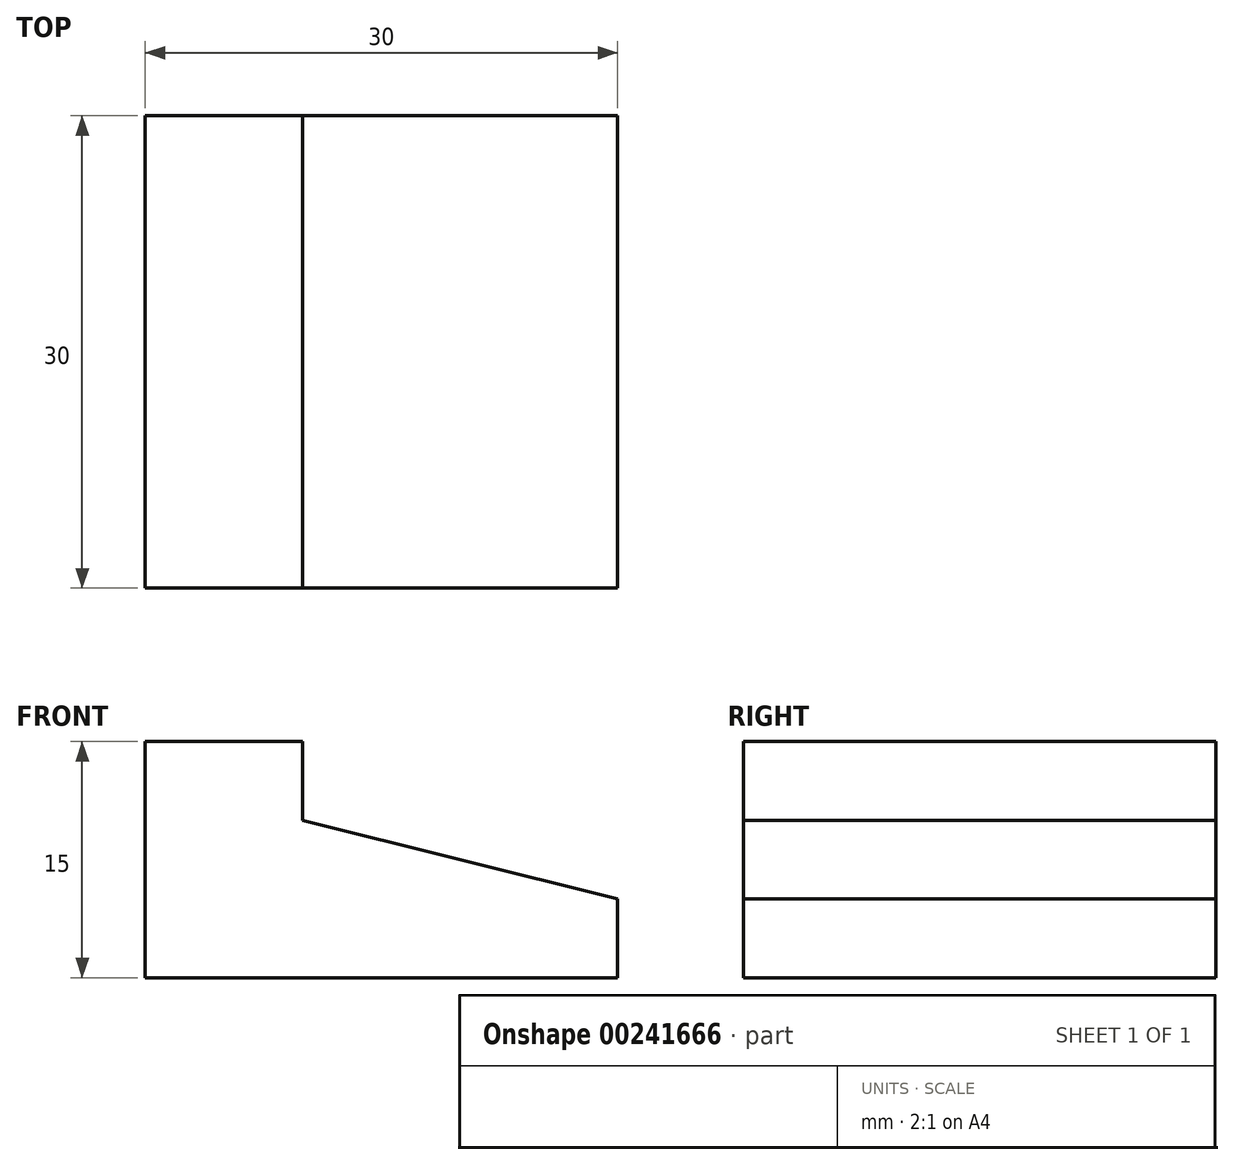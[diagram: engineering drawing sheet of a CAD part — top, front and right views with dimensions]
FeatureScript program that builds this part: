
annotation { "Feature Type Name" : "Feature", "Feature Type Description" : "" }
export const myFeature = defineFeature(function(context is Context, id is Id, definition is map)
    precondition{}
    {
        {
            var Q0;
            Q0=qCreatedBy(makeId("Top.planeOp"),FACE);
            var sketch = newSketch(context, id + "F0", { "sketchPlane" : qUnion([Q0])});
            skLineSegment(sketch, "E0.bottom", {"start": v(1.67, -3.94) * mm, "end": v(31.67, -3.94) * mm});
            skLineSegment(sketch, "E0.top", {"start": v(1.67, -33.94) * mm, "end": v(31.67, -33.94) * mm});
            skLineSegment(sketch, "E0.left", {"start": v(1.67, -3.94) * mm, "end": v(1.67, -33.94) * mm});
            skLineSegment(sketch, "E0.right", {"start": v(31.67, -3.94) * mm, "end": v(31.67, -33.94) * mm});
            skSolve(sketch);
        }
        {
            var Q0;
            Q0=makeQuery(id+"F0.imprint","IMPRINT",FACE,{"disambiguationData":[TD([[makeQuery(id+"F0.imprint","IMPRINT",EDGE,{"derivedFrom":sQuery(id+"F0.wireOp",EDGE,"E0.bottom")}),-1.0]])]});
            extrude(context, id + "F1", {"entities" : qUnion([Q0]), "depth" : 15 * mm});
        }
        {
            var Q0;
            Q0=makeQuery(id+"F1.opExtrude","SWEPT_FACE",FACE,{"disambiguationData":[OSD([sQuery(id+"F0.wireOp",EDGE,"E0.top")])]});
            var sketch = newSketch(context, id + "F2", { "sketchPlane" : qUnion([Q0])});
            skLineSegment(sketch, "E1", {"start": v(31.67, 0) * mm, "end": v(31.67, 5) * mm});
            skLineSegment(sketch, "E2", {"start": v(11.67, 10) * mm, "end": v(31.67, 5) * mm});
            skLineSegment(sketch, "E3", {"start": v(11.67, 10) * mm, "end": v(11.67, 15) * mm});
            skLineSegment(sketch, "E4", {"start": v(11.67, 15) * mm, "end": v(11.67, 10) * mm});
            skLineSegment(sketch, "E5", {"start": v(1.67, 15) * mm, "end": v(11.67, 15) * mm});
            skSolve(sketch);
        }
        {
            var Q0;
            {var subQ0=sQuery(id+"F2.wireOp",EDGE,"E2");Q0=makeQuery(id+"F2.imprint","IMPRINT",FACE,{"disambiguationData":[TD([[makeQuery(id+"F2.imprint","IMPRINT",EDGE,{"derivedFrom":subQ0}),1.0]])]});}
            extrude(context, id + "F3", {"entities" : qUnion([Q0]), "operationType" : NewBodyOperationType.REMOVE, "endBound" : BoundingType.THROUGH_ALL, "oppositeDirection" : true, "depth" : 25 * mm});
        }
    });
